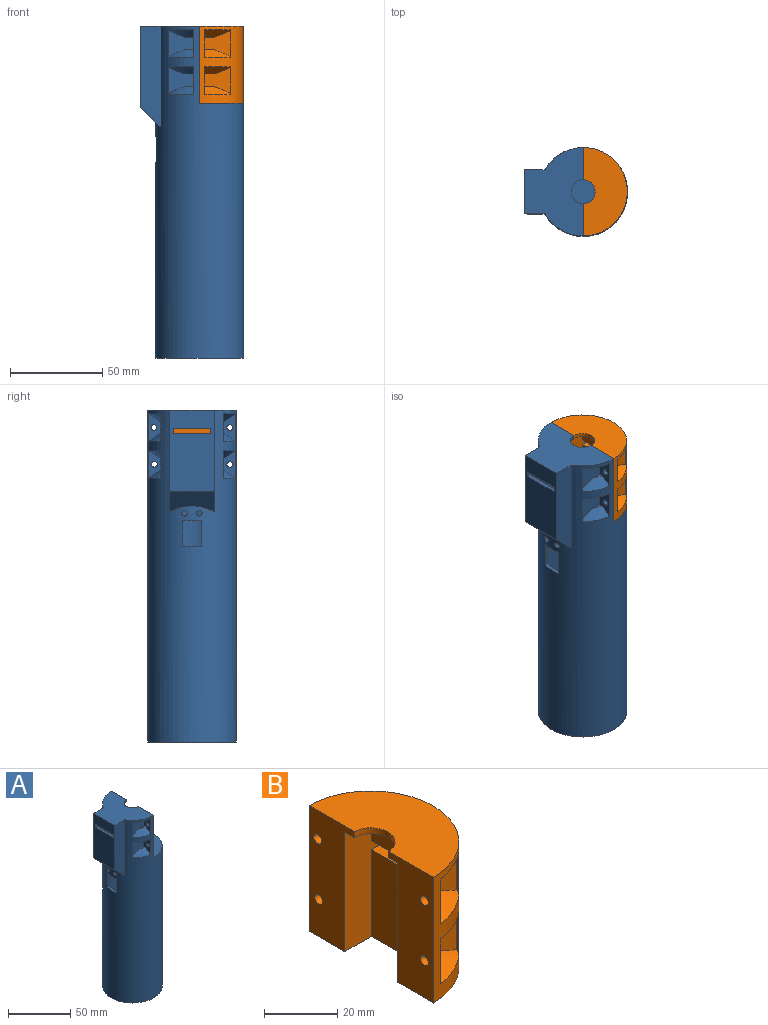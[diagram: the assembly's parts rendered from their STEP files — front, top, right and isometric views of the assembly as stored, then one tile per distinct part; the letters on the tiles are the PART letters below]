
ASSEMBLY  parts=2 mates=1
PART A: 58 faces, bbox 56.5x48.5x180.5 mm
  f0: plane 14x2.06mm, normal (0,-1,0), area 28.8mm2, adj f1,f3,f31,f56
  f1: plane 10.6x2.65mm, normal (0,0,-1), area 21.4mm2, adj f0,f2,f31,f56
  f2: plane 14x2.06mm, normal (0,1,0), area 28.8mm2, adj f1,f3,f31,f56
  f3: plane 10.6x2.65mm, normal (0,0,1), area 21.4mm2, adj f0,f2,f31,f56
  f4: cylinder r=1.5mm len=3mm, axis (-1,0,0), area 21.3mm2, adj f31,f56
  f5: cylinder r=1.5mm len=3mm, axis (-1,0,0), area 16.5mm2, adj f31,f56
  f6: cone r=21mm half-angle=56.3deg, axis (0,0,1), area 83.2mm2, adj f7,f31,f38,f39,f40
  f7: plane 5.25x1.75mm, normal (0,0,-1), area 5.4mm2, adj f6,f38,f40
  f8: cone r=21mm half-angle=56.3deg, axis (0,0,-1), area 83.2mm2, adj f9,f31,f38,f39,f40
  f9: plane 5.25x1.75mm, normal (0,0,1), area 5.4mm2, adj f8,f38,f40
  f10: cone r=21mm half-angle=56.3deg, axis (0,0,1), area 83.2mm2, adj f11,f31,f35,f36,f37
  f11: plane 5.25x1.75mm, normal (0,0,-1), area 5.4mm2, adj f10,f35,f37
  f12: cone r=21mm half-angle=56.3deg, axis (0,0,-1), area 83.2mm2, adj f13,f31,f35,f36,f37
  f13: plane 5.25x1.75mm, normal (0,0,1), area 5.4mm2, adj f12,f35,f37
  f14: cone r=21mm half-angle=56.3deg, axis (0,0,-1), area 83.2mm2, adj f15,f27,f28,f29,f31
  f15: plane 5.25x1.75mm, normal (0,0,1), area 5.4mm2, adj f14,f27,f29
  f16: cone r=21mm half-angle=56.3deg, axis (0,0,1), area 83.2mm2, adj f17,f27,f28,f29,f31
  f17: plane 5.25x1.75mm, normal (0,0,-1), area 5.4mm2, adj f16,f27,f29
  f18: cone r=21mm half-angle=56.3deg, axis (0,0,1), area 83.2mm2, adj f19,f24,f25,f26,f31
  f19: plane 5.25x1.75mm, normal (0,0,-1), area 5.4mm2, adj f18,f24,f26
  f20: cone r=21mm half-angle=56.3deg, axis (0,0,-1), area 83.2mm2, adj f21,f24,f25,f26,f31
  f21: plane 5.25x1.75mm, normal (0,0,1), area 5.4mm2, adj f20,f24,f26
  f22: cylinder r=1.55mm len=3.1mm, axis (-1,0,0), area 29.2mm2, adj f24,f55
  f23: cylinder r=1.55mm len=3.1mm, axis (-1,0,0), area 29.2mm2, adj f27,f55
  f24: plane 15.53x8.34mm, normal (-1,0,0), area 71.4mm2, adj f18,f19,f20,f21,f22,f26,f31
  f25: plane 15.01x0.96mm, normal (1,0,0), area 13.7mm2, adj f18,f20,f26,f31
  f26: plane 14.13x14mm, normal (0,1,0), area 126.9mm2, adj f18,f19,f20,f21,f24,f25
  f27: plane 15.53x8.34mm, normal (-1,0,0), area 71.4mm2, adj f14,f15,f16,f17,f23,f29,f31
  f28: plane 15.01x0.96mm, normal (1,0,0), area 13.7mm2, adj f14,f16,f29,f31
  f29: plane 14.13x14mm, normal (0,1,0), area 126.9mm2, adj f14,f15,f16,f17,f27,f28
  f30: plane 24x11.22mm, normal (-0.71,0,-0.71), area 306.9mm2, adj f31,f50,f51,f52
  f31: cylinder r=24mm len=180mm, axis (0,0,1), area 21524mm2, adj f0,f1,f2,f3,f4,f5,f6,f8
  f32: plane 44x44mm, normal (0,0,-1), area 1520.5mm2, adj f56
  f33: cylinder r=1.55mm len=3.1mm, axis (-1,0,0), area 29.2mm2, adj f35,f43
  f34: cylinder r=1.55mm len=3.1mm, axis (-1,0,0), area 29.2mm2, adj f38,f43
  f35: plane 15.53x8.34mm, normal (-1,0,0), area 71.4mm2, adj f10,f11,f12,f13,f31,f33,f37
  f36: plane 15.01x0.96mm, normal (1,0,0), area 13.7mm2, adj f10,f12,f31,f37
  f37: plane 14.13x14mm, normal (0,-1,0), area 126.9mm2, adj f10,f11,f12,f13,f35,f36
  f38: plane 15.53x8.34mm, normal (-1,0,0), area 71.4mm2, adj f6,f7,f8,f9,f31,f34,f40
  f39: plane 15.01x0.96mm, normal (1,0,0), area 13.7mm2, adj f6,f8,f31,f40
  f40: plane 14.13x14mm, normal (0,-1,0), area 126.9mm2, adj f6,f7,f8,f9,f38,f39
  f41: cylinder r=6.6mm len=13.2mm, axis (0,0,-1), area 41.5mm2, adj f42,f43,f54,f55
  f42: plane 30x20.5mm, normal (0,0,-1), area 546.6mm2, adj f41,f43,f46,f48,f53,f55
  f43: plane 42x17.4mm, normal (1,0,0), area 569.7mm2, adj f31,f33,f34,f41,f42,f47,f53,f54
  f44: plane 20.5x2mm, normal (0,0,1), area 41mm2, adj f48,f49,f50,f53
  f45: plane 20.5x2mm, normal (0,0,-1), area 41mm2, adj f46,f48,f50,f53
  f46: plane 20.5x8mm, normal (1,0,0), area 164mm2, adj f42,f45,f48,f53
  f47: plane 54x48mm, normal (0,0,1), area 1519.8mm2, adj f31,f43,f48,f49,f53,f55
  f48: plane 40x32mm, normal (0,-1,0), area 1206mm2, adj f42,f44,f45,f46,f47,f49,f50,f55
  f49: plane 29x20.5mm, normal (1,0,0), area 594.5mm2, adj f44,f47,f48,f53
  f50: plane 44x24mm, normal (-1,0,0), area 994.5mm2, adj f30,f44,f45,f48,f51,f52,f53,f54
  f51: plane 55.22x11.22mm, normal (0,1,0), area 556.4mm2, adj f30,f31,f50,f54
  f52: plane 55.22x11.22mm, normal (0,-1,0), area 556.4mm2, adj f30,f31,f50,f54
  f53: plane 40x32mm, normal (0,1,0), area 1206mm2, adj f42,f43,f44,f45,f46,f47,f49,f50
  f54: plane 48x32mm, normal (0,0,1), area 1053.3mm2, adj f31,f41,f43,f50,f51,f52,f55
  f55: plane 42x17.4mm, normal (1,0,0), area 569.7mm2, adj f22,f23,f31,f41,f42,f47,f48,f54
  f56: cylinder r=22mm len=135mm, axis (0,0,1), area 18495.4mm2, adj f0,f1,f2,f3,f4,f5,f32,f57
  f57: plane 48x48mm, normal (0,0,-1), area 289mm2, adj f31,f56
PART B: 46 faces, bbox 23.8x48x41.9 mm
  f0: cone r=21mm half-angle=56.3deg, axis (0,0,1), area 83.5mm2, adj f1,f26,f27,f28,f44
  f1: plane 5.25x1.75mm, normal (0,0,-1), area 5.4mm2, adj f0,f26,f28
  f2: cone r=21mm half-angle=56.3deg, axis (0,0,-1), area 83.5mm2, adj f3,f26,f27,f28,f44
  f3: plane 5.25x1.75mm, normal (0,0,1), area 5.4mm2, adj f2,f26,f28
  f4: cone r=21mm half-angle=56.3deg, axis (0,0,1), area 83.5mm2, adj f5,f29,f30,f31,f44
  f5: plane 5.25x1.75mm, normal (0,0,-1), area 5.4mm2, adj f4,f29,f31
  f6: cone r=21mm half-angle=56.3deg, axis (0,0,-1), area 83.5mm2, adj f7,f29,f30,f31,f44
  f7: plane 5.25x1.75mm, normal (0,0,1), area 5.4mm2, adj f6,f29,f31
  f8: cone r=21mm half-angle=56.3deg, axis (0,0,1), area 83.5mm2, adj f9,f21,f22,f23,f44
  f9: plane 5.25x1.75mm, normal (0,0,-1), area 5.4mm2, adj f8,f22,f23
  f10: cone r=21mm half-angle=56.3deg, axis (0,0,-1), area 83.5mm2, adj f11,f21,f22,f23,f44
  f11: plane 5.25x1.75mm, normal (0,0,1), area 5.4mm2, adj f10,f22,f23
  f12: cone r=21mm half-angle=56.3deg, axis (0,0,1), area 83.5mm2, adj f13,f18,f19,f20,f44
  f13: plane 5.25x1.75mm, normal (0,0,-1), area 5.4mm2, adj f12,f18,f20
  f14: cone r=21mm half-angle=56.3deg, axis (0,0,-1), area 83.5mm2, adj f15,f18,f19,f20,f44
  f15: plane 5.25x1.75mm, normal (0,0,1), area 5.4mm2, adj f14,f18,f20
  f16: cylinder r=1.55mm len=3.1mm, axis (-1,0,0), area 27.3mm2, adj f18,f43
  f17: cylinder r=1.55mm len=3.1mm, axis (-1,0,0), area 27.3mm2, adj f22,f43
  f18: plane 15x7.81mm, normal (1,0,0), area 71.4mm2, adj f12,f13,f14,f15,f16,f20,f44
  f19: plane 15.01x0.96mm, normal (-1,0,0), area 13.7mm2, adj f12,f14,f20,f44
  f20: plane 14.13x14mm, normal (0,1,0), area 126.9mm2, adj f12,f13,f14,f15,f18,f19
  f21: plane 15.01x0.96mm, normal (-1,0,0), area 13.7mm2, adj f8,f10,f23,f44
  f22: plane 15x7.81mm, normal (1,0,0), area 71.4mm2, adj f8,f9,f10,f11,f17,f23,f44
  f23: plane 14.13x14mm, normal (0,1,0), area 126.9mm2, adj f8,f9,f10,f11,f21,f22
  f24: cylinder r=1.55mm len=3.1mm, axis (-1,0,0), area 27.3mm2, adj f29,f34
  f25: cylinder r=1.55mm len=3.1mm, axis (-1,0,0), area 27.3mm2, adj f26,f34
  f26: plane 15x7.81mm, normal (1,0,0), area 71.4mm2, adj f0,f1,f2,f3,f25,f28,f44
  f27: plane 15.01x0.96mm, normal (-1,0,0), area 13.7mm2, adj f0,f2,f28,f44
  f28: plane 14.13x14mm, normal (0,-1,0), area 126.9mm2, adj f0,f1,f2,f3,f26,f27
  f29: plane 15x7.81mm, normal (1,0,0), area 71.4mm2, adj f4,f5,f6,f7,f24,f31,f44
  f30: plane 15.01x0.96mm, normal (-1,0,0), area 13.7mm2, adj f4,f6,f31,f44
  f31: plane 14.13x14mm, normal (0,-1,0), area 126.9mm2, adj f4,f5,f6,f7,f29,f30
  f32: cylinder r=6.6mm len=13.19mm, axis (0,0,-1), area 40.7mm2, adj f33,f34,f42,f43
  f33: plane 48x23.8mm, normal (0,0,1), area 829.4mm2, adj f32,f34,f43,f44
  f34: plane 41.9x17.4mm, normal (-1,0,0), area 568.3mm2, adj f24,f25,f32,f33,f41,f42,f44,f45
  f35: plane 20.5x7.5mm, normal (0,0,-1), area 153.7mm2, adj f37,f38,f40,f41
  f36: plane 20.5x7.5mm, normal (0,0,1), area 153.8mm2, adj f37,f38,f39,f41
  f37: plane 20.5x3mm, normal (-1,0,0), area 61.5mm2, adj f35,f36,f38,f41
  f38: plane 39.9x17.8mm, normal (0,-1,0), area 433.5mm2, adj f35,f36,f37,f39,f40,f42,f43,f45
  f39: plane 28.9x20.5mm, normal (-1,0,0), area 592.5mm2, adj f36,f38,f41,f45
  f40: plane 20.5x8mm, normal (-1,0,0), area 164mm2, adj f35,f38,f41,f42
  f41: plane 39.9x17.8mm, normal (0,1,0), area 433.5mm2, adj f34,f35,f36,f37,f39,f40,f42,f45
  f42: plane 20.5x10.3mm, normal (0,0,-1), area 145.4mm2, adj f32,f34,f38,f40,f41,f43
  f43: plane 41.9x17.4mm, normal (-1,0,0), area 568.3mm2, adj f16,f17,f32,f33,f38,f42,f44,f45
  f44: cylinder r=24mm len=48mm, axis (0,0,1), area 2189.4mm2, adj f0,f2,f4,f6,f8,f10,f12,f14
  f45: plane 48x23.8mm, normal (0,0,-1), area 684mm2, adj f34,f38,f39,f41,f43,f44
PLACE A t=(-97.57,7.51,-73.59)mm
PLACE B t=(-97.77,7.51,-73.59)mm
MATE fastened A.f34 <-> B.f25  axis (1,0,0) through (-97.57,-12.9,96.87)mm
